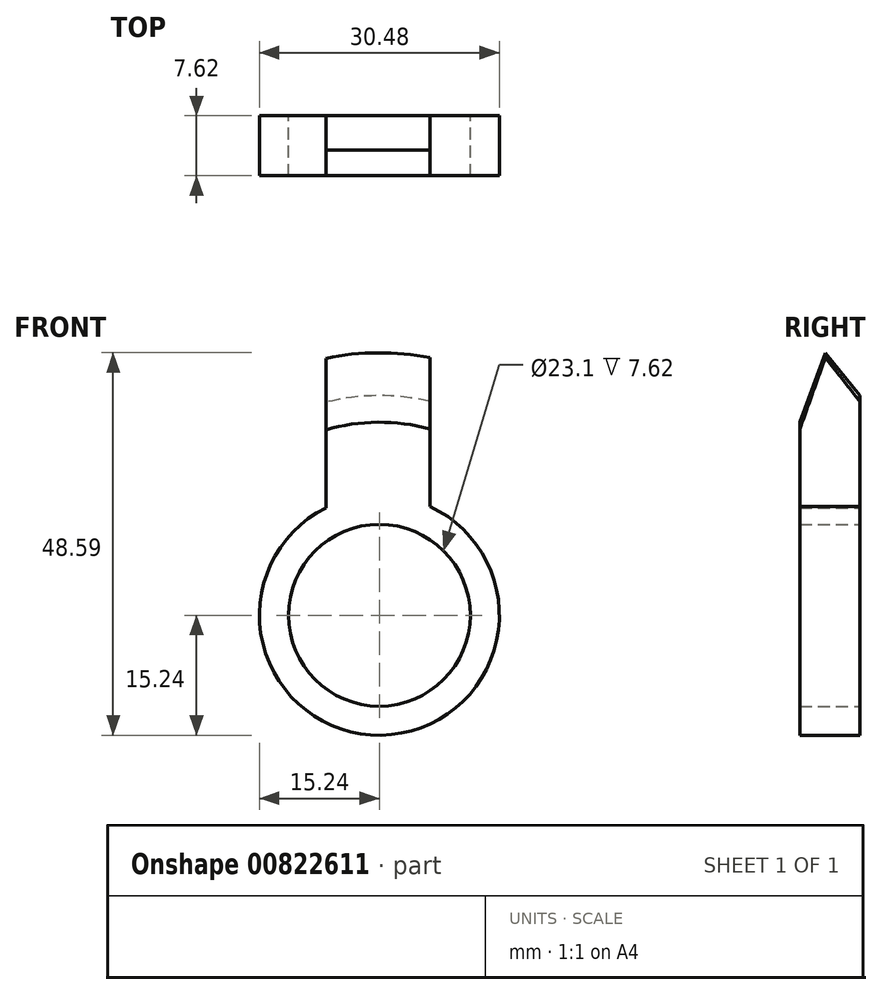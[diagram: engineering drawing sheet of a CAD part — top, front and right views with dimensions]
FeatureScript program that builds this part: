
annotation { "Feature Type Name" : "Feature", "Feature Type Description" : "" }
export const myFeature = defineFeature(function(context is Context, id is Id, definition is map)
    precondition{}
    {
        {
            var Q0;
            Q0=qCreatedBy(makeId("Front.planeOp"),FACE);
            var sketch = newSketch(context, id + "F0", { "sketchPlane" : qUnion([Q0])});
            skCircle(sketch, "E0", {"center": v(0, 0) * mm, "radius": 15.24 * mm});
            skLineSegment(sketch, "E1", {"start": v(-6.8, 13.64) * mm, "end": v(-6.8, 35.23) * mm});
            skLineSegment(sketch, "E2", {"start": v(-6.8, 35.23) * mm, "end": v(6.41, 35.23) * mm});
            skLineSegment(sketch, "E3", {"start": v(6.41, 35.23) * mm, "end": v(6.41, 13.83) * mm});
            skCircle(sketch, "E4", {"center": v(0, 0) * mm, "radius": 11.55 * mm});
            skSolve(sketch);
        }
        {
            var Q0;
            {var subQ0=sQuery(id+"F0.wireOp",EDGE,"E1");Q0=makeQuery(id+"F0.imprint","IMPRINT",FACE,{"disambiguationData":[TD([[makeQuery(id+"F0.imprint","IMPRINT",EDGE,{"derivedFrom":subQ0}),-1.0]])]});}
            var Q1;
            Q1=makeQuery(id+"F0.imprint","IMPRINT",FACE,{"disambiguationData":[TD([[makeQuery(id+"F0.imprint","IMPRINT",EDGE,{"derivedFrom":sQuery(id+"F0.wireOp",EDGE,"E4")}),-1.0]])]});
            var Q2;
            {var subQ0=sQuery(id+"FwLVLBxUmEVC1ga_0.1.F0.wireOp",EDGE,"E1");Q2=makeQuery(id+"FwLVLBxUmEVC1ga_0.1.F0.imprint","IMPRINT",FACE,{"disambiguationData":[TD([[makeQuery(id+"FwLVLBxUmEVC1ga_0.1.F0.imprint","IMPRINT",EDGE,{"derivedFrom":subQ0}),-1.0]])]});}
            var Q3;
            {var subQ0=sQuery(id+"FwLVLBxUmEVC1ga_0.2.F0.wireOp",EDGE,"E1");Q3=makeQuery(id+"FwLVLBxUmEVC1ga_0.2.F0.imprint","IMPRINT",FACE,{"disambiguationData":[TD([[makeQuery(id+"FwLVLBxUmEVC1ga_0.2.F0.imprint","IMPRINT",EDGE,{"derivedFrom":subQ0}),-1.0]])]});}
            extrude(context, id + "F1", {"entities" : qUnion([Q0, Q1, Q2, Q3]), "depth" : 7.62 * mm, "offsetDistance" : 25.4 * mm});
        }
        {
            var Q0;
            Q0=qCreatedBy(makeId("Top.planeOp"),FACE);
            var sketch = newSketch(context, id + "F2", { "sketchPlane" : qUnion([Q0])});
            skLineSegment(sketch, "E5", {"start": v(-23.58, 3.49) * mm, "end": v(-33.35, -4.4) * mm});
            skLineSegment(sketch, "E6", {"start": v(-33.35, -4.4) * mm, "end": v(-15.85, -10.8) * mm});
            skLineSegment(sketch, "E7", {"start": v(-15.85, -10.8) * mm, "end": v(-36.36, -11.35) * mm});
            skLineSegment(sketch, "E8", {"start": v(-36.36, -11.35) * mm, "end": v(-36.36, 4.78) * mm});
            skLineSegment(sketch, "E9", {"start": v(-36.36, 4.78) * mm, "end": v(-23.58, 3.49) * mm});
            skSolve(sketch);
        }
        {
            var Q0;
            Q0=makeQuery(id+"F2.imprint","IMPRINT",FACE,{"disambiguationData":[TD([[makeQuery(id+"F2.imprint","IMPRINT",EDGE,{"derivedFrom":sQuery(id+"F2.wireOp",EDGE,"E5")}),-1.0]])]});
            var Q1;
            Q1=makeQuery(id+"F1.opExtrude","CAP_EDGE",EDGE,{"disambiguationData":[OSD([sQuery(id+"F0.wireOp",EDGE,"E4")])],"isStart":true});
            revolve(context, id + "F3", {"operationType" : NewBodyOperationType.REMOVE, "surfaceOperationType" : NewSurfaceOperationType.NEW, "entities" : qUnion([Q0]), "axis" : qUnion([Q1]), "revolveType" : RevolveType.FULL, "oppositeDirection" : true});
        }
    });
